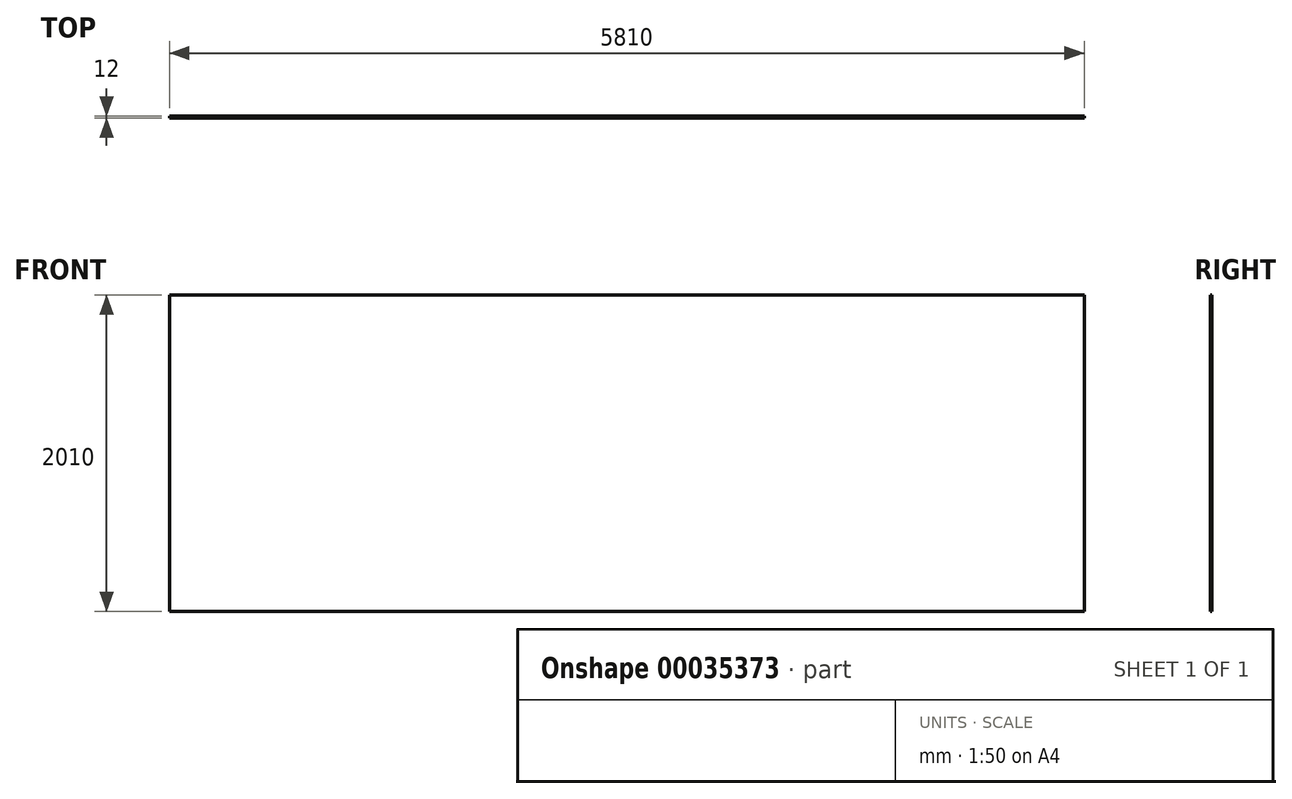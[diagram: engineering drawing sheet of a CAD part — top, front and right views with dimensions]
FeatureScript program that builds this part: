
annotation { "Feature Type Name" : "Feature", "Feature Type Description" : "" }
export const myFeature = defineFeature(function(context is Context, id is Id, definition is map)
    precondition{}
    {
        {
            var Q0;
            Q0=qCreatedBy(makeId("Front.planeOp"),FACE);
            var sketch = newSketch(context, id + "F0", { "sketchPlane" : qUnion([Q0])});
            skLineSegment(sketch, "E0.rect.bottom", {"start": v(2905, -1005) * mm, "end": v(-2905, -1005) * mm});
            skLineSegment(sketch, "E0.rect.top", {"start": v(2905, 1005) * mm, "end": v(-2905, 1005) * mm});
            skLineSegment(sketch, "E0.rect.left", {"start": v(2905, -1005) * mm, "end": v(2905, 1005) * mm});
            skLineSegment(sketch, "E0.rect.right", {"start": v(-2905, -1005) * mm, "end": v(-2905, 1005) * mm});
            skPoint(sketch, "E0.rect.middle", {"position": v(0, 0) * mm});
            skSolve(sketch);
        }
        {
            var Q0;
            Q0=makeQuery(id+"F0.imprint","IMPRINT",FACE,{"disambiguationData":[TD([[makeQuery(id+"F0.imprint","IMPRINT",EDGE,{"derivedFrom":sQuery(id+"F0.wireOp",EDGE,"E0.rect.bottom")}),-1.0]])]});
            extrude(context, id + "F1", {"entities" : qUnion([Q0]), "depth" : 12 * mm});
        }
    });
